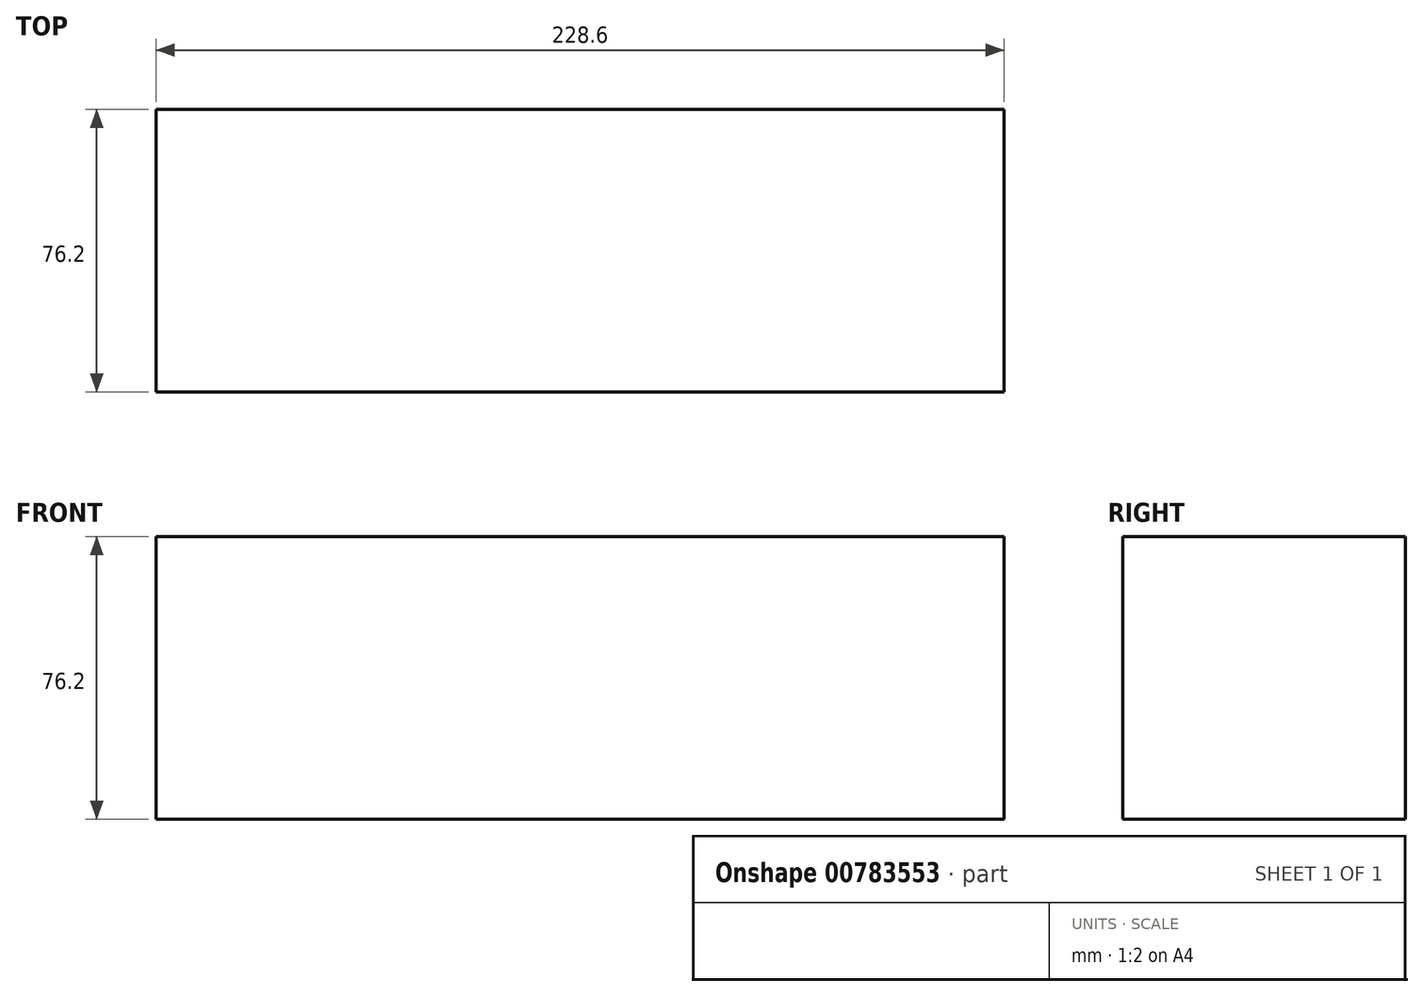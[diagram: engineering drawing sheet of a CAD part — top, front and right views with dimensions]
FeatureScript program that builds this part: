
annotation { "Feature Type Name" : "Feature", "Feature Type Description" : "" }
export const myFeature = defineFeature(function(context is Context, id is Id, definition is map)
    precondition{}
    {
        {
            var Q0;
            Q0=qCreatedBy(makeId("Front.planeOp"),FACE);
            var sketch = newSketch(context, id + "F0", { "sketchPlane" : qUnion([Q0])});
            skLineSegment(sketch, "E0.bottom", {"start": v(30.34, 0) * mm, "end": v(106.54, 0) * mm});
            skLineSegment(sketch, "E0.top", {"start": v(30.34, 76.2) * mm, "end": v(106.54, 76.2) * mm});
            skLineSegment(sketch, "E0.left", {"start": v(30.34, 0) * mm, "end": v(30.34, 76.2) * mm});
            skLineSegment(sketch, "E0.right", {"start": v(106.54, 0) * mm, "end": v(106.54, 76.2) * mm});
            skLineSegment(sketch, "E1.bottom", {"start": v(106.54, 76.2) * mm, "end": v(182.74, 76.2) * mm});
            skLineSegment(sketch, "E1.top", {"start": v(106.54, 0) * mm, "end": v(182.74, 0) * mm});
            skLineSegment(sketch, "E1.left", {"start": v(106.54, 76.2) * mm, "end": v(106.54, 0) * mm});
            skLineSegment(sketch, "E1.right", {"start": v(182.74, 76.2) * mm, "end": v(182.74, 0) * mm});
            skLineSegment(sketch, "E2.bottom", {"start": v(30.34, 76.2) * mm, "end": v(-45.86, 76.2) * mm});
            skLineSegment(sketch, "E2.top", {"start": v(30.34, 0) * mm, "end": v(-45.86, 0) * mm});
            skLineSegment(sketch, "E2.left", {"start": v(30.34, 76.2) * mm, "end": v(30.34, 0) * mm});
            skLineSegment(sketch, "E2.right", {"start": v(-45.86, 76.2) * mm, "end": v(-45.86, 0) * mm});
            skLineSegment(sketch, "E3.bottom", {"start": v(-45.86, 76.2) * mm, "end": v(30.34, 76.2) * mm});
            skLineSegment(sketch, "E3.top", {"start": v(-45.86, 152.4) * mm, "end": v(30.34, 152.4) * mm});
            skLineSegment(sketch, "E3.left", {"start": v(-45.86, 76.2) * mm, "end": v(-45.86, 152.4) * mm});
            skLineSegment(sketch, "E3.right", {"start": v(30.34, 76.2) * mm, "end": v(30.34, 152.4) * mm});
            skLineSegment(sketch, "E4.top", {"start": v(106.54, 152.4) * mm, "end": v(182.74, 152.4) * mm});
            skLineSegment(sketch, "E4.left", {"start": v(106.54, 76.2) * mm, "end": v(106.54, 152.4) * mm});
            skLineSegment(sketch, "E4.right", {"start": v(182.74, 76.2) * mm, "end": v(182.74, 152.4) * mm});
            skSolve(sketch);
        }
        {
            var Q0;
            Q0=makeQuery(id+"F0.imprint","IMPRINT",FACE,{"disambiguationData":[TD([[makeQuery(id+"F0.imprint","IMPRINT",EDGE,{"derivedFrom":sQuery(id+"F0.wireOp",EDGE,"E2.top")}),-1.0]])]});
            var Q1;
            Q1=makeQuery(id+"F0.imprint","IMPRINT",FACE,{"disambiguationData":[TD([[makeQuery(id+"F0.imprint","IMPRINT",EDGE,{"derivedFrom":sQuery(id+"F0.wireOp",EDGE,"E3.bottom")}),1.0]])]});
            var Q2;
            Q2=makeQuery(id+"F0.imprint","IMPRINT",FACE,{"disambiguationData":[TD([[makeQuery(id+"F0.imprint","IMPRINT",EDGE,{"derivedFrom":sQuery(id+"F0.wireOp",EDGE,"E0.bottom")}),1.0]])]});
            var Q3;
            Q3=makeQuery(id+"F0.imprint","IMPRINT",FACE,{"disambiguationData":[TD([[makeQuery(id+"F0.imprint","IMPRINT",EDGE,{"derivedFrom":sQuery(id+"F0.wireOp",EDGE,"E1.top")}),1.0]])]});
            var Q4;
            Q4=makeQuery(id+"F0.imprint","IMPRINT",FACE,{"disambiguationData":[TD([[makeQuery(id+"F0.imprint","IMPRINT",EDGE,{"derivedFrom":sQuery(id+"F0.wireOp",EDGE,"E1.bottom")}),1.0]])]});
            extrude(context, id + "F1", {"entities" : qUnion([Q0, Q1, Q2, Q3, Q4]), "endBound" : BoundingType.SYMMETRIC, "depth" : 76.2 * mm, "offsetDistance" : 25.4 * mm});
        }
    });
